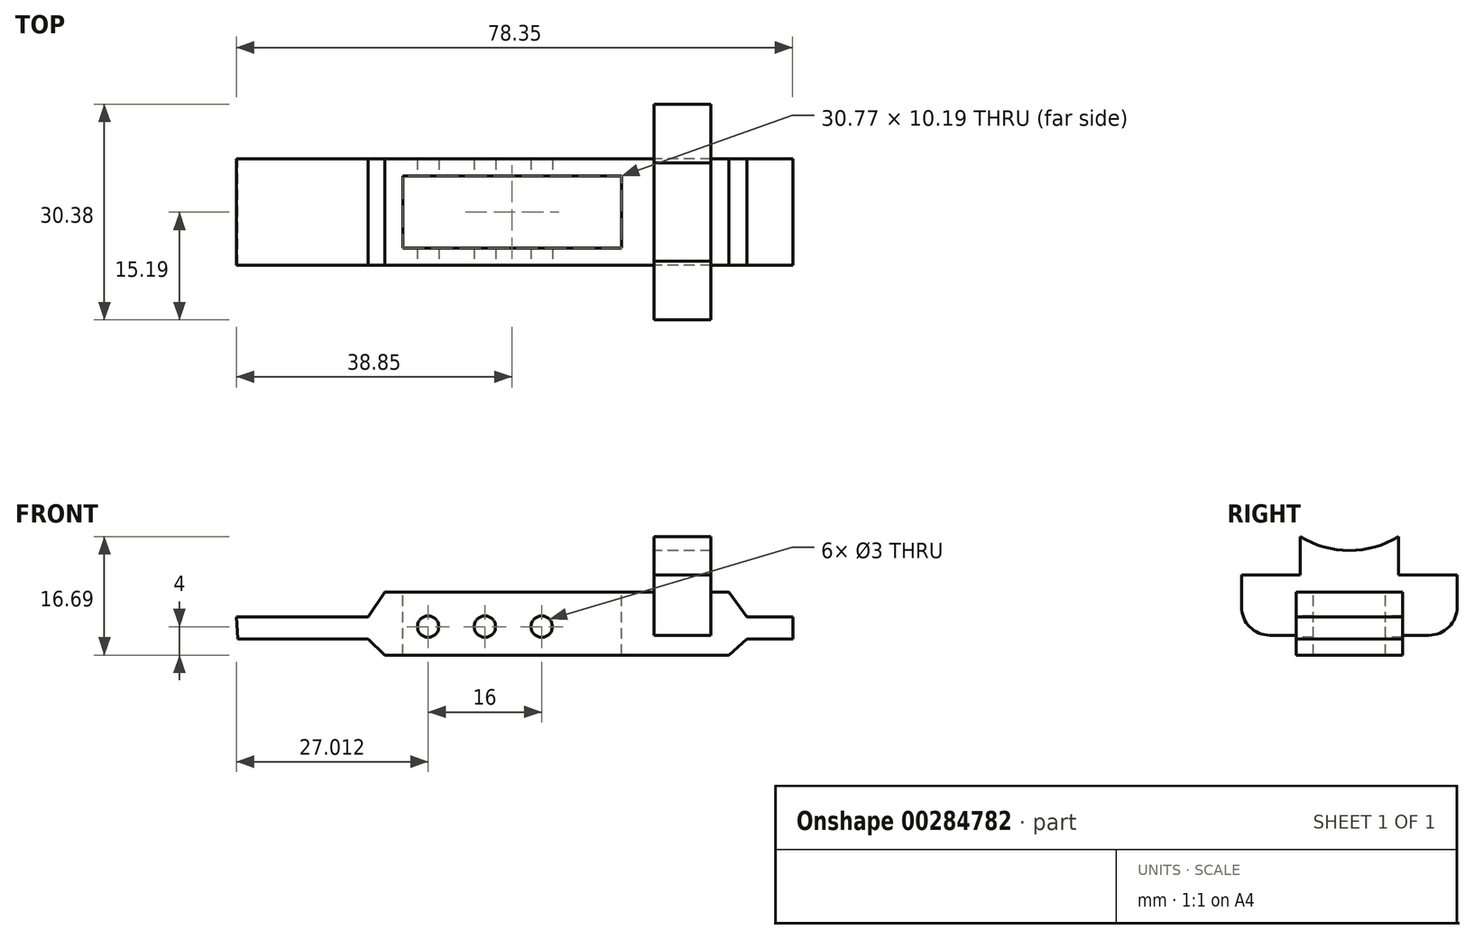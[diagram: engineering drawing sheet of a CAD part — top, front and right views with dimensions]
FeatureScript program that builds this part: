
annotation { "Feature Type Name" : "Feature", "Feature Type Description" : "" }
export const myFeature = defineFeature(function(context is Context, id is Id, definition is map)
    precondition{}
    {
        {
            var Q0;
            Q0=qCreatedBy(makeId("Front.planeOp"),FACE);
            var sketch = newSketch(context, id + "F0", { "sketchPlane" : qUnion([Q0])});
            skLineSegment(sketch, "E0", {"start": v(-48.85, 5.37) * mm, "end": v(-30.28, 5.37) * mm});
            skLineSegment(sketch, "E1", {"start": v(-30.28, 5.37) * mm, "end": v(-27.94, 8.9) * mm});
            skLineSegment(sketch, "E2", {"start": v(-27.94, 8.9) * mm, "end": v(20.52, 8.9) * mm});
            skLineSegment(sketch, "E3", {"start": v(20.52, 8.9) * mm, "end": v(23.06, 5.37) * mm});
            skLineSegment(sketch, "E4", {"start": v(23.06, 5.37) * mm, "end": v(29.5, 5.37) * mm});
            skLineSegment(sketch, "E5", {"start": v(29.5, 5.37) * mm, "end": v(29.5, 2.25) * mm});
            skLineSegment(sketch, "E6", {"start": v(29.5, 2.25) * mm, "end": v(23.06, 2.25) * mm});
            skLineSegment(sketch, "E7", {"start": v(23.06, 2.25) * mm, "end": v(20.52, 0) * mm});
            skLineSegment(sketch, "E8", {"start": v(20.52, 0) * mm, "end": v(-27.94, 0) * mm});
            skLineSegment(sketch, "E9", {"start": v(-27.94, 0) * mm, "end": v(-30.28, 2.25) * mm});
            skLineSegment(sketch, "E10", {"start": v(-30.28, 2.25) * mm, "end": v(-48.65, 2.25) * mm});
            skLineSegment(sketch, "E11", {"start": v(-48.65, 2.25) * mm, "end": v(-48.85, 5.37) * mm});
            skSolve(sketch);
        }
        {
            var Q0;
            Q0=makeQuery(id+"F0.imprint","IMPRINT",FACE,{"disambiguationData":[TD([[makeQuery(id+"F0.imprint","IMPRINT",EDGE,{"derivedFrom":sQuery(id+"F0.wireOp",EDGE,"E0")}),-1.0]])]});
            extrude(context, id + "F1", {"entities" : qUnion([Q0]), "endBound" : BoundingType.SYMMETRIC, "depth" : 15 * mm});
        }
        {
            var Q0;
            Q0=makeQuery(id+"F1.opExtrude","SWEPT_FACE",FACE,{"disambiguationData":[OSD([sQuery(id+"F0.wireOp",EDGE,"E2")])]});
            var sketch = newSketch(context, id + "F2", { "sketchPlane" : qUnion([Q0])});
            skLineSegment(sketch, "E12.bottom", {"start": v(-25.38, 5.1) * mm, "end": v(5.38, 5.1) * mm});
            skLineSegment(sketch, "E12.top", {"start": v(-25.38, -5.1) * mm, "end": v(5.38, -5.1) * mm});
            skLineSegment(sketch, "E12.left", {"start": v(-25.38, 5.1) * mm, "end": v(-25.38, -5.1) * mm});
            skLineSegment(sketch, "E12.right", {"start": v(5.38, 5.1) * mm, "end": v(5.38, -5.1) * mm});
            skPoint(sketch, "E12.middle", {"position": v(-10, 0) * mm});
            skSolve(sketch);
        }
        {
            var Q0;
            Q0=makeQuery(id+"F2.imprint","IMPRINT",FACE,{"disambiguationData":[TD([[makeQuery(id+"F2.imprint","IMPRINT",EDGE,{"derivedFrom":sQuery(id+"F2.wireOp",EDGE,"E12.bottom")}),-1.0]])]});
            extrude(context, id + "F3", {"entities" : qUnion([Q0]), "operationType" : NewBodyOperationType.REMOVE, "endBound" : BoundingType.THROUGH_ALL, "oppositeDirection" : true, "depth" : 25 * mm});
        }
        {
            var Q0;
            Q0=qCreatedBy(makeId("Right.planeOp"),FACE);
            cPlane(context, id + "F4", {"entities" : qUnion([Q0]), "cplaneType" : CPlaneType.OFFSET, "offset" : 10 * mm, "width" : 150 * mm, "height" : 150 * mm});
        }
        {
            var Q0;
            Q0=qCreatedBy(id+"F4.planeOp",FACE);
            var sketch = newSketch(context, id + "F5", { "sketchPlane" : qUnion([Q0])});
            skLineSegment(sketch, "E13.bottom", {"start": v(-11.2, 2.79) * mm, "end": v(11.2, 2.79) * mm});
            skLineSegment(sketch, "E13.top", {"start": v(-15.2, 11.25) * mm, "end": v(-6.92, 11.25) * mm});
            skLineSegment(sketch, "E13.left", {"start": v(-15.2, 6.79) * mm, "end": v(-15.2, 11.25) * mm});
            skLineSegment(sketch, "E13.right", {"start": v(15.2, 6.79) * mm, "end": v(15.2, 11.25) * mm});
            skPoint(sketch, "E13.middle", {"position": v(0, 7.02) * mm});
            skPoint(sketch, "E14.visualSharp", {"position": v(-15.2, 2.79) * mm});
            skArc(sketch, "E14.filletArc", {"start": v(-15.2, 6.79) * mm, "mid": v(-14.02, 3.96) * mm, "end": v(-11.2, 2.79) * mm});
            skPoint(sketch, "E15.visualSharp", {"position": v(15.2, 2.79) * mm});
            skArc(sketch, "E15.filletArc", {"start": v(11.2, 2.79) * mm, "mid": v(14.02, 3.96) * mm, "end": v(15.2, 6.79) * mm});
            skLineSegment(sketch, "E16.left", {"start": v(6.92, 16.7) * mm, "end": v(6.92, 11.25) * mm});
            skLineSegment(sketch, "E16.right", {"start": v(-6.92, 16.7) * mm, "end": v(-6.92, 11.25) * mm});
            skPoint(sketch, "E16.middle", {"position": v(0, 14.71) * mm});
            skArc(sketch, "E17", {"start": v(-6.92, 16.7) * mm, "mid": v(0, 14.71) * mm, "end": v(6.92, 16.7) * mm});
            skPoint(sketch, "E18.orphan", {"position": v(-6.92, 18.17) * mm});
            skPoint(sketch, "E19.orphan", {"position": v(6.92, 18.17) * mm});
            skLineSegment(sketch, "E20.trimOffspring", {"start": v(6.92, 11.25) * mm, "end": v(15.2, 11.25) * mm});
            skSolve(sketch);
        }
        {
            var Q0;
            Q0=makeQuery(id+"F5.imprint","IMPRINT",FACE,{"disambiguationData":[TD([[makeQuery(id+"F5.imprint","IMPRINT",EDGE,{"derivedFrom":sQuery(id+"F5.wireOp",EDGE,"E13.bottom")}),1.0]])]});
            extrude(context, id + "F6", {"entities" : qUnion([Q0]), "operationType" : NewBodyOperationType.ADD, "depth" : 8 * mm});
        }
        {
            var Q0;
            Q0=makeQuery(id+"F1.opExtrude","CAP_FACE",FACE,{"disambiguationData":[OSD([sQuery(id+"F0.wireOp",EDGE,"E0"),sQuery(id+"F0.wireOp",EDGE,"E1"),sQuery(id+"F0.wireOp",EDGE,"E2"),sQuery(id+"F0.wireOp",EDGE,"E3"),sQuery(id+"F0.wireOp",EDGE,"E4"),sQuery(id+"F0.wireOp",EDGE,"E5"),sQuery(id+"F0.wireOp",EDGE,"E6"),sQuery(id+"F0.wireOp",EDGE,"E7"),sQuery(id+"F0.wireOp",EDGE,"E8"),sQuery(id+"F0.wireOp",EDGE,"E9"),sQuery(id+"F0.wireOp",EDGE,"E10"),sQuery(id+"F0.wireOp",EDGE,"E11")])],"isStart":false});
            var sketch = newSketch(context, id + "F7", { "sketchPlane" : qUnion([Q0])});
            skCircle(sketch, "E21", {"center": v(-21.84, 4) * mm, "radius": 1.5 * mm});
            skCircle(sketch, "E22", {"center": v(-13.84, 4) * mm, "radius": 1.5 * mm});
            skCircle(sketch, "E23", {"center": v(-5.84, 4) * mm, "radius": 1.5 * mm});
            skSolve(sketch);
        }
        {
            var Q0;
            Q0 = qSketchRegion(id + "F7", true);
            extrude(context, id + "F8", {"entities" : qUnion([Q0]), "operationType" : NewBodyOperationType.REMOVE, "endBound" : BoundingType.THROUGH_ALL, "oppositeDirection" : true, "depth" : 25 * mm});
        }
    });
